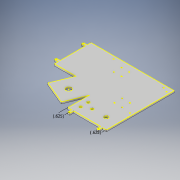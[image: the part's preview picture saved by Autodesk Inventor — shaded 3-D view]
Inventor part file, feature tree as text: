
AUTODESK INVENTOR PART (.ipt)
format: ipt  version: 2018 (Build 220112000, 112)  size: 290,816 bytes
history: native  units: in
note: dims shown in document units (in); Inventor stores cm internally (conversion verified against a paired STEP export)
features: sketch x11, extrude x10, projected_geometry x4
ambient origin geometry x8: Origin, YZ Plane, XZ Plane, XY Plane, X Axis, Y Axis, Z Axis, Center Point
bodies: Solid1 (feature_tree)
feature tree (25):
  extrude  "Extrusion1"  Depth=4.75in
  extrude  "Extrusion2"  Depth=6.0in
  extrude  "Extrusion3"  Depth=0.25in TaperAngle=0.0deg
  extrude  "Extrusion4"  Depth=2.8in TaperAngle=0.0deg
  extrude  "Extrusion5"  Depth=0.25in
  extrude  "Extrusion6"  Depth=0.125in
  extrude  "Extrusion7"  Depth=0.5in
  extrude  "Extrusion8"  Depth=0.5in
  extrude  "Extrusion9"  Depth=0.25in
  extrude  "Extrusion10"  Depth=0.5in
  sketch  "Sketch13"  dims[d36=0.11in d37=0.125in d38=0.125in d39=0.25in d40=0.5in d41=0.11in d42=0.125in d43=0.125in d44=0.0in d45=0.5in d46=0.25in d47=0.0in d48=0.11in d49=0.11in d50=0.11in d51=0.11in d52=1.0in d53=1.0in d54=1.0in d55=1.0in d56=1.0in d57=1.0in d58=0.75in d59=1.5in d60=0.11in d61=0.11in d62=0.11in d63=0.11in d64=1.0in d65=1.0in d66=1.0in d67=1.0in d68=1.0in d69=1.0in d70=0.25in d71=0.0in d72=0.12in d73=0.12in d74=0.625in d75=4.75in d76=0.365in d77=0.365in d78=0.12in d79=0.12in d80=0.365in d81=1.0in d82=0.5in d83=0.365in d84=0.25in d85=0.0in d86=0.335in d87=0.335in d88=0.335in d89=0.69in d90=0.9in d91=0.9in d92=1.4in d93=1.75in d94=0.75in d95=0.75in d96=0.25in d97=0.0in d98=0.5in d99=0.25in d100=0.0in d101=3.5in d102=0.625in d103=0.625in]
  sketch  "Sketch1"  dims[d0=8.0in d1=4.75in]
  sketch  "Sketch3"  dims[d2=5.0in d3=6.0in]
  projected_geometry  "Projected Loop1"
  sketch  "Sketch4"  dims[d4=0.25in d5=0.0in d6=2.8in d7=0.0in]
  projected_geometry  "Projected Loop2"
  sketch  "Sketch5"  dims[d8=2.8in d9=0.0in d10=2.8in d11=0.0in]
  projected_geometry  "Projected Loop3"
  sketch  "Sketch7"  dims[d13=0.5in d14=0.25in]
  sketch  "Sketch8"  dims[d15=0.11in d16=0.125in]
  sketch  "Sketch9"  dims[d17=0.5in d18=0.125in]
  sketch  "Sketch10"  dims[d19=0.5in d20=0.25in d21=0.11in d22=0.125in d23=0.125in d24=0.0in d25=0.5in]
  sketch  "Sketch11"  dims[d26=0.25in d27=0.0in d33=0.25in]
  sketch  "Sketch12"  dims[d34=0.5in d35=0.5in]
  projected_geometry  "Projected Loop5"
